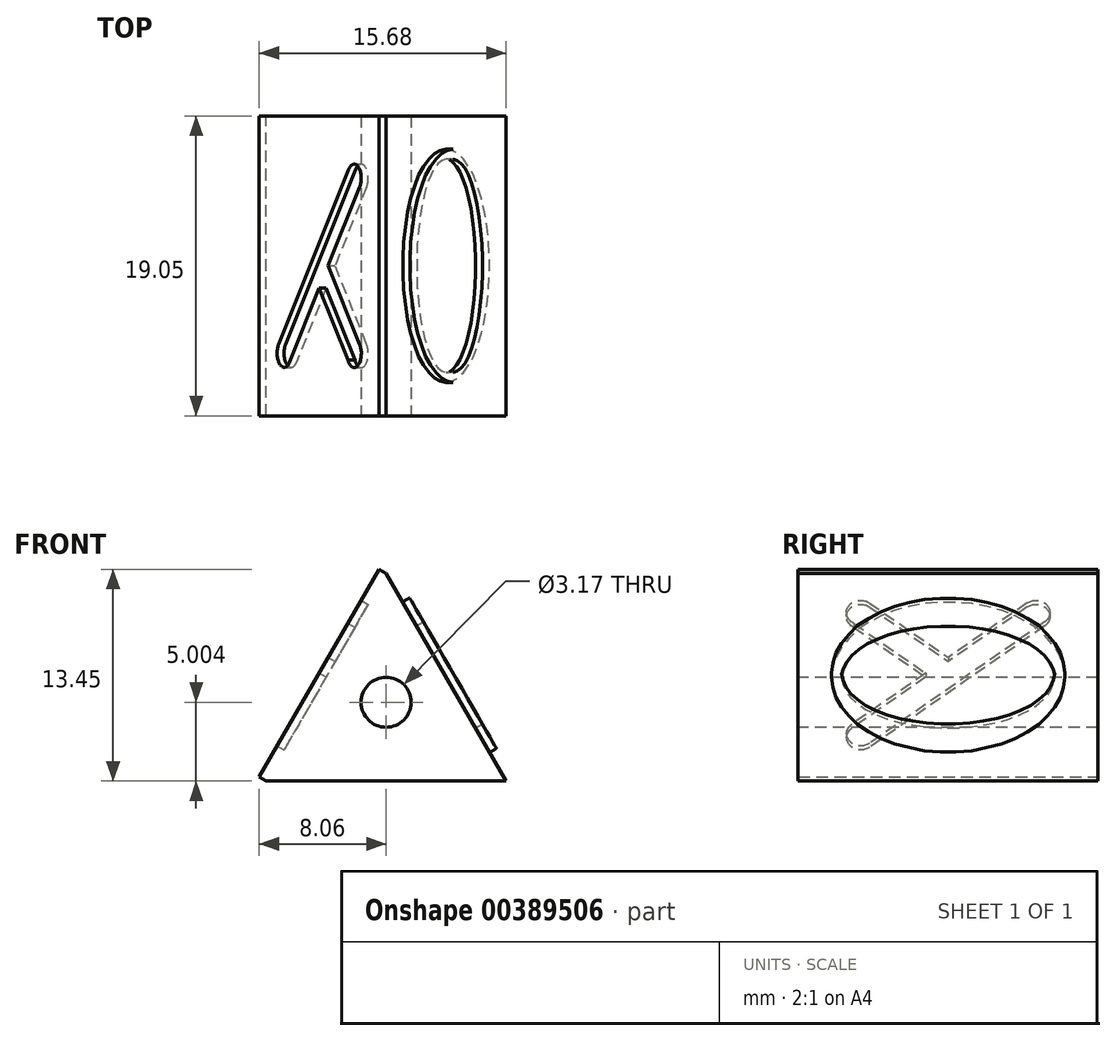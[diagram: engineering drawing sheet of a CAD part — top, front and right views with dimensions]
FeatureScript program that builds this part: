
annotation { "Feature Type Name" : "Feature", "Feature Type Description" : "" }
export const myFeature = defineFeature(function(context is Context, id is Id, definition is map)
    precondition{}
    {
        {
            var Q0;
            Q0=qCreatedBy(makeId("Front.planeOp"),FACE);
            var sketch = newSketch(context, id + "F0", { "sketchPlane" : qUnion([Q0])});
            skLineSegment(sketch, "E0", {"start": v(-7.62, 0) * mm, "end": v(0, 13.2) * mm});
            skLineSegment(sketch, "E1", {"start": v(0, 13.2) * mm, "end": v(7.62, 0) * mm});
            skLineSegment(sketch, "E2", {"start": v(-7.62, 0) * mm, "end": v(7.62, 0) * mm});
            skSolve(sketch);
        }
        {
            var Q0;
            Q0=makeQuery(id+"F0.imprint","IMPRINT",FACE,{"disambiguationData":[TD([[makeQuery(id+"F0.imprint","IMPRINT",EDGE,{"derivedFrom":sQuery(id+"F0.wireOp",EDGE,"E0")}),-1.0]])]});
            extrude(context, id + "F1", {"entities" : qUnion([Q0]), "depth" : 19.05 * mm});
        }
        {
            var Q0;
            Q0=makeQuery(id+"F1.opExtrude","SWEPT_FACE",FACE,{"disambiguationData":[OSD([sQuery(id+"F0.wireOp",EDGE,"E1")])]});
            var sketch = newSketch(context, id + "F2", { "sketchPlane" : qUnion([Q0])});
            skEllipse(sketch, "E3", {"center": v(-9.53, 3.8) * mm, "majorRadius": 7.43 * mm, "minorRadius": 5.52 * mm, "majorAxis": v(1, 0)});
            skEllipse(sketch, "E4", {"center": v(-9.53, 3.8) * mm, "majorRadius": 6.78 * mm, "minorRadius": 3.75 * mm, "majorAxis": v(-1, 0)});
            skSolve(sketch);
        }
        {
            var Q0;
            Q0=makeQuery(id+"F2.imprint","IMPRINT",FACE,{"disambiguationData":[TD([[makeQuery(id+"F2.imprint","IMPRINT",EDGE,{"derivedFrom":sQuery(id+"F2.wireOp",EDGE,"E3")}),1.0]])]});
            var sketch = newSketch(context, id + "F3", { "sketchPlane" : qUnion([Q0])});
            skSolve(sketch);
        }
        {
            var Q0;
            Q0 = qSketchRegion(id + "F3", true);
            var Q1;
            Q1=makeQuery(id+"F2.imprint","IMPRINT",FACE,{"disambiguationData":[TD([[makeQuery(id+"F2.imprint","IMPRINT",EDGE,{"derivedFrom":sQuery(id+"F2.wireOp",EDGE,"E3")}),1.0]])]});
            extrude(context, id + "F4", {"entities" : qUnion([Q0, Q1]), "operationType" : NewBodyOperationType.ADD, "depth" : 0.5 * mm});
        }
        {
            var Q0;
            Q0=makeQuery(id+"F1.opExtrude","SWEPT_FACE",FACE,{"disambiguationData":[OSD([sQuery(id+"F0.wireOp",EDGE,"E0")])]});
            var sketch = newSketch(context, id + "F5", { "sketchPlane" : qUnion([Q0])});
            skLineSegment(sketch, "E5", {"start": v(4.52, 8.95) * mm, "end": v(15.64, 0.06) * mm});
            skLineSegment(sketch, "E6", {"start": v(3.4, 7.55) * mm, "end": v(14.52, -1.34) * mm});
            skArc(sketch, "E7", {"start": v(3.4, 7.55) * mm, "mid": v(3.26, 8.81) * mm, "end": v(4.52, 8.95) * mm});
            skArc(sketch, "E8", {"start": v(14.52, -1.34) * mm, "mid": v(15.78, -1.2) * mm, "end": v(15.64, 0.06) * mm});
            skLineSegment(sketch, "E9", {"start": v(15.51, 7.46) * mm, "end": v(4.52, -1.33) * mm});
            skLineSegment(sketch, "E10", {"start": v(14.52, 8.96) * mm, "end": v(3.4, 0.06) * mm});
            skArc(sketch, "E11", {"start": v(14.52, 8.96) * mm, "mid": v(15.84, 8.75) * mm, "end": v(15.51, 7.46) * mm});
            skArc(sketch, "E12", {"start": v(3.4, 0.06) * mm, "mid": v(3.26, -1.2) * mm, "end": v(4.52, -1.33) * mm});
            skSolve(sketch);
        }
        {
            var Q0;
            {var subQ5=sQuery(id+"F5.wireOp",EDGE,"E12");Q0=makeQuery(id+"F5.imprint","IMPRINT",FACE,{"disambiguationData":[TD([[makeQuery(id+"F5.imprint","IMPRINT",EDGE,{"derivedFrom":subQ5}),1.0]])]});}
            var Q1;
            {var subQ0=sQuery(id+"F5.wireOp",EDGE,"E8");Q1=makeQuery(id+"F5.imprint","IMPRINT",FACE,{"disambiguationData":[TD([[makeQuery(id+"F5.imprint","IMPRINT",EDGE,{"derivedFrom":subQ0}),1.0]])]});}
            var Q2;
            {var subQ5=sQuery(id+"F5.wireOp",EDGE,"E11");Q2=makeQuery(id+"F5.imprint","IMPRINT",FACE,{"disambiguationData":[TD([[makeQuery(id+"F5.imprint","IMPRINT",EDGE,{"derivedFrom":subQ5}),-1.0]])]});}
            var Q3;
            {var subQ0=sQuery(id+"F5.wireOp",EDGE,"E7");Q3=makeQuery(id+"F5.imprint","IMPRINT",FACE,{"disambiguationData":[TD([[makeQuery(id+"F5.imprint","IMPRINT",EDGE,{"derivedFrom":subQ0}),-1.0]])]});}
            var Q4;
            {var subQ0=sQuery(id+"F5.wireOp",EDGE,"E10");var subQ1=sQuery(id+"F5.wireOp",EDGE,"E5");var subQ2=makeQuery(id+"F5.imprint","INTERSECT",VERTEX,{"derivedFrom":[subQ1,subQ0]});Q4=makeQuery(id+"F5.imprint","IMPRINT",FACE,{"disambiguationData":[TD([[makeQuery(id+"F5.imprint","IMPRINT",EDGE,{"disambiguationData":[TD([[subQ2,-1.0]])],"derivedFrom":subQ1}),-1.0]])]});}
            extrude(context, id + "F6", {"entities" : qUnion([Q0, Q1, Q2, Q3, Q4]), "operationType" : NewBodyOperationType.ADD, "depth" : 0.5 * mm});
        }
        {
            var Q0;
            Q0=makeQuery(id+"F1.opExtrude","CAP_FACE",FACE,{"disambiguationData":[OSD([sQuery(id+"F0.wireOp",EDGE,"E0"),sQuery(id+"F0.wireOp",EDGE,"E1"),sQuery(id+"F0.wireOp",EDGE,"E2")])],"isStart":false});
            var sketch = newSketch(context, id + "F7", { "sketchPlane" : qUnion([Q0])});
            skCircle(sketch, "E13", {"center": v(0, 5) * mm, "radius": 1.59 * mm});
            skSolve(sketch);
        }
        {
            var Q0;
            Q0=makeQuery(id+"F7.imprint","IMPRINT",FACE,{"disambiguationData":[TD([[makeQuery(id+"F7.imprint","IMPRINT",EDGE,{"derivedFrom":sQuery(id+"F7.wireOp",EDGE,"E13")}),1.0]])]});
            var Q1;
            Q1=sQuery(id+"F7.wireOp",EDGE,"E13");
            extrude(context, id + "F8", {"entities" : qUnion([Q0]), "operationType" : NewBodyOperationType.REMOVE, "surfaceEntities" : qUnion([Q1]), "oppositeDirection" : true, "depth" : 25.4 * mm});
        }
    });
